FCSTD DOCUMENT  (FreeCAD 1.0R39109 (Git))
Label: Rotor_Mold_Assembly
License: All rights reserved
LicenseURL: http://en.wikipedia.org/wiki/All_rights_reserved
objects: App::Link×8, Part::FeaturePython×3, Spreadsheet::Sheet×1, App::Part×1
EXTERNAL_REF file=Rotor_Mold_Lid.FCStd obj=PocketBody
EXTERNAL_REF file=../../../Master_of_Puppets.FCStd obj=Alternator
EXTERNAL_REF file=../../../Master_of_Puppets.FCStd obj=Hub
EXTERNAL_REF file=../../../Master_of_Puppets.FCStd obj=Spreadsheet
EXTERNAL_REF file=Rotor_Mold_Base.FCStd obj=PolarPatternBody
EXTERNAL_REF file=Rotor_Mold_Surround.FCStd obj=PolarPatternBody
EXTERNAL_REF file=Rotor_Mold_Island.FCStd obj=PocketBody
EXTERNAL_REF file=../Rotor_Back.FCStd obj=Part
EXTERNAL_REF file=../../../Fasteners/Fastener_Bolt_HubHoles.FCStd obj=Binder
EXTERNAL_REF file=../../../Fasteners/Fastener_HexNut_HubHoles.FCStd obj=Binder
EXTERNAL_REF file=../../../Fasteners/Fastener_WoodScrew_RotorMold.FCStd obj=Part

FEATURE [App::Link] Link  label="Rotor_Mold_Lid"
  LinkPlacement = pos=(0,0,35) rot=(0,0,1;0rad)
  LinkedObject = -> <external Rotor_Mold_Lid.FCStd>#PocketBody
  Placement = pos=(0,0,35) rot=(0,0,1;0rad)
  expr: .Placement.Base.z = Spreadsheet.LidZ
  expr: Visibility = Spreadsheet.ShowLid
FEATURE [Spreadsheet::Sheet] Spreadsheet
  cells = A1='Inputs; A2='RotorDiskRadius; B2(RotorDiskRadius)==Master_of_Puppets#Spreadsheet.RotorDiskRadius; A3='MagnetThickness; B3(MagnetThickness)==Master_of_Puppets#Spreadsheet.MagnetThickness; A4='RotorDiskThickness; B4(RotorDiskThickness)==Master_of_Puppets#Spreadsheet.RotorDiskThickness; A5='HubPitchCircleRadius; B5(HubPitchCircleRadius)==Master_of_Puppets#Hub.HubPitchCircleRadius; A6='MagnetMaterial; B6(MagnetMaterial)==Master_of_Puppets#Spreadsheet.MagnetMaterial; A7='RotorMoldBaseThickness; B7(RotorMoldBaseThickness)==Master_of_Puppets#Alternator.RotorMoldBaseThickness; A8='NumberOfRotorMoldBolts; B8(NumberOfRotorMoldBolts)==Master_of_Puppets#Alternator.NumberOfRotorMoldBolts; A9='RotorMoldScrewHolesCircumradius; B9(RotorMoldScrewHolesCircumradius)==Master_of_Puppets#Alternator.RotorMoldScrewHolesCircumradius; A10='NumberOfRotorMoldScrews; B10(NumberOfRotorMoldScrews)==Master_of_Puppets#Alternator.NumberOfRotorMoldScrews; A11='RotorMoldSurroundThickness; B11(RotorMoldSurroundThickness)==Master_of_Puppets#Alternator.RotorMoldSurroundThickness; A12='RotorMoldScrewLength; B12(RotorMoldScrewLength)==Master_of_Puppets#Alternator.RotorMoldScrewLength; A13='Calculated; A14='DistanceBetweenLayers; B14(DistanceBetweenLayers)=0; C14='Increase to see space between parts.; A15='SurroundZ; B15(SurroundZ)==RotorMoldBaseThickness + DistanceBetweenLayers; A16='IslandZ; B16(IslandZ)==SurroundZ + RotorDiskThickness; A17='ScrewZ; B17(ScrewZ)==SurroundZ + RotorMoldSurroundThickness - RotorMoldScrewLength; A18='LidZ; B18(LidZ)==IslandZ + MagnetThickness + DistanceBetweenLayers; A19='ShowLid; B19(ShowLid)==MagnetMaterial != <<Ferrite C8>> ? 1 : 0; A20='NutsZ; B20(NutsZ)==ShowLid == 1 ? LidZ : SurroundZ + RotorMoldSurroundThickness
FEATURE [App::Link] Link001  label="Rotor_Mold_Base"
  LinkedObject = -> <external Rotor_Mold_Base.FCStd>#PolarPatternBody
FEATURE [App::Link] Link002  label="Rotor_Mold_Surround"
  LinkPlacement = pos=(0,0,15) rot=(0,0,1;0rad)
  LinkedObject = -> <external Rotor_Mold_Surround.FCStd>#PolarPatternBody
  Placement = pos=(0,0,15) rot=(0,0,1;0rad)
  expr: .Placement.Base.z = Spreadsheet.SurroundZ
FEATURE [App::Link] Link003  label="Rotor_Mold_Island"
  LinkPlacement = pos=(0,0,25) rot=(0,0,1;0rad)
  LinkedObject = -> <external Rotor_Mold_Island.FCStd>#PocketBody
  Placement = pos=(0,0,25) rot=(0,0,1;0rad)
  expr: .Placement.Base.z = Spreadsheet.IslandZ
FEATURE [App::Link] Link004  label="Rotor"
  LinkPlacement = pos=(0,0,15) rot=(0,0,1;0rad)
  LinkedObject = -> <external ../Rotor_Back.FCStd>#Part
  Placement = pos=(0,0,15) rot=(0,0,1;0rad)
  expr: .Placement.Base.z = Spreadsheet.SurroundZ
FEATURE [App::Link] Link005  label="Fastener_Bolt_HubHoles"
  LinkPlacement = pos=(0,50,0) rot=(0,0,1;0rad)
  LinkedObject = -> <external ../../../Fasteners/Fastener_Bolt_HubHoles.FCStd>#Binder
  Placement = pos=(0,50,0) rot=(0,0,1;0rad)
  Scale = -1
  ScaleVector = (-1,-1,-1)
  expr: .Placement.Base.y = Spreadsheet.HubPitchCircleRadius
FEATURE [Part::FeaturePython] Array  label="Bolts"  # Draft array (typed FeaturePython)
  AlwaysSyncPlacement = false
  Angle = 360
  ArrayType = 1
  Axis = (0,0,1)
  Base = -> Link005
  Center = (0,0,0)
  Count = 2
  ExpandArray = false
  Fuse = false
  IntervalAxis = (0,0,0)
  IntervalX = (50,0,0)
  IntervalY = (0,50,0)
  IntervalZ = (0,0,50)
  NumberCircles = 3
  NumberPolar = 2
  NumberX = 2
  NumberY = 2
  NumberZ = 1
  PlacementList = 2 placements: [(0,50,0),(-6.12323e-15,-50,0)]
  RadialDistance = 50
  ScaleList = (2) [(1,1,1),(1,1,1)]
  Symmetry = 1
  TangentialDistance = 25
  expr: NumberPolar = Spreadsheet.NumberOfRotorMoldBolts
FEATURE [App::Link] Link006  label="Fastener_HexNut"
  LinkPlacement = pos=(0,50,0) rot=(0,0,1;0rad)
  LinkedObject = -> <external ../../../Fasteners/Fastener_HexNut_HubHoles.FCStd>#Binder
  Placement = pos=(0,50,0) rot=(0,0,1;0rad)
  expr: .Placement.Base.y = Spreadsheet.HubPitchCircleRadius
FEATURE [Part::FeaturePython] Array001  label="Nuts"  # Draft array (typed FeaturePython)
  AlwaysSyncPlacement = false
  Angle = 360
  ArrayType = 1
  Axis = (0,0,1)
  Base = -> Link006
  Center = (0,0,0)
  Count = 2
  ExpandArray = false
  Fuse = false
  IntervalAxis = (0,0,0)
  IntervalX = (50,0,0)
  IntervalY = (0,50,0)
  IntervalZ = (0,0,50)
  NumberCircles = 3
  NumberPolar = 2
  NumberX = 2
  NumberY = 2
  NumberZ = 1
  Placement = pos=(0,0,35) rot=(0,0,1;0rad)
  PlacementList = 2 placements: [(0,50,0),(-6.12323e-15,-50,0)]
  RadialDistance = 50
  ScaleList = (2) [(1,1,1),(1,1,1)]
  Symmetry = 1
  TangentialDistance = 25
  expr: .Placement.Base.z = Spreadsheet.NutsZ
  expr: NumberPolar = Spreadsheet.NumberOfRotorMoldBolts
FEATURE [App::Link] Link007  label="Fastener_WoodScrew_RotorMold"
  LinkPlacement = pos=(0,176.7,0) rot=(0,0,1;0rad)
  LinkedObject = -> <external ../../../Fasteners/Fastener_WoodScrew_RotorMold.FCStd>#Part
  Placement = pos=(0,176.7,0) rot=(0,0,1;0rad)
  expr: .Placement.Base.y = Spreadsheet.RotorMoldScrewHolesCircumradius
  expr: .Placement.Base.z = Spreadsheet.ScrewZ
FEATURE [Part::FeaturePython] Array002  label="Screws"  # Draft array (typed FeaturePython)
  AlwaysSyncPlacement = false
  Angle = 360
  ArrayType = 1
  Axis = (0,0,1)
  Base = -> Link007
  Center = (0,0,0)
  Count = 9
  ExpandArray = false
  Fuse = false
  IntervalAxis = (0,0,0)
  IntervalX = (50,0,0)
  IntervalY = (0,50,0)
  IntervalZ = (0,0,50)
  NumberCircles = 3
  NumberPolar = 9
  NumberX = 2
  NumberY = 2
  NumberZ = 1
  PlacementList = 9 placements: [(0,176.7,0),(-113.581,135.36,0),(-174.016,30.6836,0),(-153.027,-88.35,0),(-60.435,-166.044,0),(60.435,-166.044,0),(153.027,-88.35,0),(174.016,30.6836,0),(113.581,135.36,0)]
  RadialDistance = 50
  ScaleList = (9) [(1,1,1),(1,1,1),(1,1,1),(1,1,1),(1,1,1),(1,1,1),(1,1,1),(1,1,1),(1,1,1)]
  Symmetry = 1
  TangentialDistance = 25
  expr: NumberPolar = Spreadsheet.NumberOfRotorMoldScrews
FEATURE [App::Part] Part  label="Rotor_Mold_Assembly"
  Group = -> [Link001,Link002,Link003,Link004,Link,Link005,Array,Link006,Array001,Link007,Array002]
  Origin = -> Origin

RESOLVED EXTERNAL PARTS (link-assembly join: the EXTERNAL_REF files above that resolve inside this repo's crawl, each included once):
---- part ../../../Fasteners/Fastener_Bolt_HubHoles.FCStd = doc fcstd_15687eb65cfb ----
FCSTD DOCUMENT  (FreeCAD 0.20R29177 (Git))
Label: Fastener_Bolt_HubHoles
License: All rights reserved
LicenseURL: http://en.wikipedia.org/wiki/All_rights_reserved
objects: PartDesign::SubShapeBinder×1
note: 1 computed .brp shape members not serialized (recipe doc carries the construction recipe); baked Part::Feature solids carry a one-line shape summary decoded from their .brp
EXTERNAL_REF file=Fastener_Bolt_Tail_Vane.FCStd obj=Body

FEATURE [PartDesign::SubShapeBinder] Binder  label="Fastener_Bolt_HubHoles"
  BindCopyOnChange = 2
  BindMode = 0
  ClaimChildren = false
  Fuse = false
  MakeFace = true
  OffsetFill = false
  OffsetIntersection = false
  OffsetJoinType = 0
  OffsetOpenResult = false
  PartialLoad = false
  Relative = true
  Support = -> [<external Fastener_Bolt_Tail_Vane.FCStd>#Body]
  Variant = 1
  _Version = 2
---- part ../../../Fasteners/Fastener_HexNut_HubHoles.FCStd = doc fcstd_dba15245a95b ----
FCSTD DOCUMENT  (FreeCAD 0.21R33771 (Git))
Label: Fastener_HexNut_HubHoles
License: All rights reserved
LicenseURL: http://en.wikipedia.org/wiki/All_rights_reserved
objects: PartDesign::SubShapeBinder×1
note: 1 computed .brp shape members not serialized (recipe doc carries the construction recipe); baked Part::Feature solids carry a one-line shape summary decoded from their .brp
EXTERNAL_REF file=Fastener_HexNut.FCStd obj=Body

FEATURE [PartDesign::SubShapeBinder] Binder  label="Fastener_HexNut"
  BindCopyOnChange = 2
  BindMode = 0
  ClaimChildren = false
  Fuse = false
  MakeFace = true
  OffsetFill = false
  OffsetIntersection = false
  OffsetJoinType = 0
  OffsetOpenResult = false
  PartialLoad = false
  Relative = true
  Support = -> [<external Fastener_HexNut.FCStd>#Body]
  Variant = 1
  _Version = 2
---- part ../../../Fasteners/Fastener_WoodScrew_RotorMold.FCStd = doc fcstd_a80e977c1a3f ----
FCSTD DOCUMENT  (FreeCAD 0.21R33771 (Git))
Label: Fastener_WoodScrew_RotorMold
Comment: DIN 571 Hexagon head wood screw
License: All rights reserved
LicenseURL: http://en.wikipedia.org/wiki/All_rights_reserved
objects: App::Link×1, PartDesign::SubShapeBinder×1, App::Part×1
note: 1 computed .brp shape members not serialized (recipe doc carries the construction recipe); baked Part::Feature solids carry a one-line shape summary decoded from their .brp
EXTERNAL_REF file=Fastener_WoodScrew_StatorMold.FCStd obj=Sweep
EXTERNAL_REF file=Fastener_WoodScrew_StatorMold.FCStd obj=Body

FEATURE [App::Link] Link  label="TipThreadLink"
  LinkedObject = -> <external Fastener_WoodScrew_StatorMold.FCStd>#Sweep
FEATURE [PartDesign::SubShapeBinder] Binder
  BindCopyOnChange = 2
  BindMode = 0
  ClaimChildren = false
  Context = -> Part [Binder.]
  Fuse = false
  MakeFace = true
  OffsetFill = false
  OffsetIntersection = false
  OffsetJoinType = 0
  OffsetOpenResult = false
  PartialLoad = false
  Relative = true
  Support = -> [<external Fastener_WoodScrew_StatorMold.FCStd>#Body]
  Variant = 1
  _Version = 2
FEATURE [App::Part] Part  label="Fastener_WoodScrew"
  Group = -> [Link,Binder]
  Origin = -> Origin
---- part ../../../Master_of_Puppets.FCStd = doc fcstd_6404554055c4 (61625 chars; too large to inline — full recipe in that document) ----
---- part ../Rotor_Back.FCStd = doc fcstd_8870bba639fa ----
FCSTD DOCUMENT  (FreeCAD 0.21R33675 (Git))
Label: Rotor_Back
License: All rights reserved
LicenseURL: http://en.wikipedia.org/wiki/All_rights_reserved
objects: App::Link×2, Spreadsheet::Sheet×1, App::Part×1
EXTERNAL_REF file=Rotor_Disk_Back.FCStd obj=Pocket001Body
EXTERNAL_REF file=../../Master_of_Puppets.FCStd obj=Alternator
EXTERNAL_REF file=../../Master_of_Puppets.FCStd obj=Spreadsheet
EXTERNAL_REF file=Rotor_Disk_Back_ReducedWeight.FCStd obj=Body
EXTERNAL_REF file=MagnetResin_Assembly.FCStd obj=Part

FEATURE [App::Link] Link  label="Rotor_Disk_Back"
  LinkPlacement = pos=(3.6e-15,0,0) rot=(0,0,1;0rad)
  LinkedObject = -> <external Rotor_Disk_Back.FCStd>#Pocket001Body
  Placement = pos=(3.6e-15,0,0) rot=(0,0,1;0rad)
  expr: LinkedObject = Spreadsheet.Disk
FEATURE [Spreadsheet::Sheet] Spreadsheet
  cells = A1='Inputs; A2='RotorDiskRadius; B2(RotorDiskRadius)==Master_of_Puppets#Spreadsheet.RotorDiskRadius; A3='WeightReductionRotorDiskRadiusThreshold; B3(WeightReductionRotorDiskRadiusThreshold)==Master_of_Puppets#Alternator.WeightReductionRotorDiskRadiusThreshold; A4='Disk; A5='DiskFullWeight; B5(DiskFullWeight)==<<Rotor_Disk_Back>>#<<Rotor_Disk_Back>>._self; A6='DiskReducedWeight; B6(DiskReducedWeight)==<<Rotor_Disk_Back_ReducedWeight>>#<<Rotor_Disk_Back>>._self; A7='Disk; B7(Disk)==RotorDiskRadius <= WeightReductionRotorDiskRadiusThreshold ? DiskFullWeight : DiskReducedWeight
FEATURE [App::Link] Link003  label="MagnetResin_Assembly"
  LinkedObject = -> <external MagnetResin_Assembly.FCStd>#Part
FEATURE [App::Part] Part  label="Rotor"
  Group = -> [Link,Link003]
  Origin = -> Origin
  Placement = pos=(0,0,0) rot=(0,1,0;3.14159rad)
---- part Rotor_Mold_Base.FCStd = doc fcstd_7ba465a5f749 ----
FCSTD DOCUMENT  (FreeCAD 0.20R29177 (Git))
Label: Rotor_Mold_Base
License: All rights reserved
LicenseURL: http://en.wikipedia.org/wiki/All_rights_reserved
objects: Sketcher::SketchObject×3, PartDesign::Pocket×2, PartDesign::PolarPattern×2, PartDesign::Pad×1, Spreadsheet::Sheet×1, PartDesign::Body×1
note: 12 computed .brp shape members not serialized (recipe doc carries the construction recipe); baked Part::Feature solids carry a one-line shape summary decoded from their .brp
EXTERNAL_REF file=../../../Master_of_Puppets.FCStd obj=Alternator
EXTERNAL_REF file=../../../Master_of_Puppets.FCStd obj=Hub
EXTERNAL_REF file=../../../Master_of_Puppets.FCStd obj=Spreadsheet

FEATURE [Sketcher::SketchObject] Sketch
  FullyConstrained = true
  MapMode = 5
  Support = -> [XY_Plane001]
  expr: Constraints[15] = Spreadsheet.RotorMoldSideLength
  sketch-geometry (6):
    g0: LineSegment StartX=-199.995 StartY=199.995 StartZ=0 EndX=199.995 EndY=199.995 EndZ=0
    g1: LineSegment StartX=199.995 StartY=199.995 StartZ=0 EndX=199.995 EndY=-199.995 EndZ=0
    g2: LineSegment StartX=199.995 StartY=-199.995 StartZ=0 EndX=-199.995 EndY=-199.995 EndZ=0
    g3: LineSegment StartX=-199.995 StartY=-199.995 StartZ=0 EndX=-199.995 EndY=199.995 EndZ=0
    g4: LineSegment StartX=-199.995 StartY=199.995 StartZ=0 EndX=199.995 EndY=-199.995 EndZ=0
    g5: LineSegment StartX=199.995 StartY=199.995 StartZ=0 EndX=-199.995 EndY=-199.995 EndZ=0
  constraints (16):
    c: Coincident(g0,g1)
    c: Coincident(g1,g2)
    c: Coincident(g2,g3)
    c: Coincident(g3,g0)
    c: Horizontal(g0)
    c: Horizontal(g2)
    c: Vertical(g1)
    c: Vertical(g3)
    c: Coincident(g4,g0)
    c: Coincident(g4,g1)
    c: Coincident(g5,g0)
    c: Coincident(g5,g2)
    c: PointOnObject(g-1,g5)
    c: PointOnObject(g-1,g4)
    c: Equal(g0,g3)
    c: Distance(g0) = 399.99
FEATURE [PartDesign::Pad] Pad
  AllowMultiFace = false
  Direction = (0,0,1)
  Length = 15
  Length2 = 100
  Profile = -> Sketch
  Type = 0
  expr: Length = Spreadsheet.RotorMoldBaseThickness
FEATURE [Sketcher::SketchObject] Sketch001  label="BoltHoleSketch"
  FullyConstrained = true
  MapMode = 5
  Placement = pos=(0,0,15) rot=(0,0,1;0rad)
  Support = -> [Pad]
  expr: Constraints[1] = Spreadsheet.HubPitchCircleRadius
  expr: Constraints[4] = Spreadsheet.HubHolesRadius
  sketch-geometry (2):
    g0: Circle CenterX=0 CenterY=0 CenterZ=0 NormalX=0 NormalY=0 NormalZ=1 AngleXU=0 Radius=50
    g1: Circle CenterX=0 CenterY=50 CenterZ=0 NormalX=0 NormalY=0 NormalZ=1 AngleXU=0 Radius=6
  constraints (5):
    c: Coincident(g0,g-1)
    c: Radius(g0) = 50
    c: PointOnObject(g1,g-2)
    c: PointOnObject(g1,g0)
    c: Radius(g1) = 6
FEATURE [PartDesign::Pocket] Pocket  label="BoltHolePocket"
  AllowMultiFace = false
  BaseFeature = -> Pad
  Direction = (0,0,-1)
  Length = 5
  Length2 = 100
  Profile = -> Sketch001
  Type = 1
FEATURE [Sketcher::SketchObject] Sketch002  label="ScrewHoleSketch"
  FullyConstrained = true
  MapMode = 5
  Placement = pos=(0,0,15) rot=(0,0,1;0rad)
  Support = -> [Pocket]
  expr: Constraints[1] = Spreadsheet.RotorMoldScrewHolesCircumradius
  expr: Constraints[3] = Spreadsheet.ScrewHoleRadius
  sketch-geometry (2):
    g0: Circle CenterX=0 CenterY=0 CenterZ=0 NormalX=0 NormalY=0 NormalZ=1 AngleXU=0 Radius=177
    g1: Circle CenterX=0 CenterY=177 CenterZ=0 NormalX=0 NormalY=0 NormalZ=1 AngleXU=0 Radius=2
  constraints (5):
    c: Coincident(g0,g-1)
    c: Radius(g0) = 177
    c: PointOnObject(g1,g0)
    c: Radius(g1) = 2
    c: PointOnObject(g1,g-2)
FEATURE [PartDesign::Pocket] Pocket001  label="ScrewHolePocket"
  AllowMultiFace = false
  BaseFeature = -> Pocket
  Direction = (0,0,-1)
  Length = 5
  Length2 = 100
  Profile = -> Sketch002
  Type = 1
FEATURE [PartDesign::PolarPattern] PolarPattern  label="ScrewHolePolarPattern"
  Angle = 360
  Axis = -> Sketch002 [N_Axis]
  BaseFeature = -> Pocket001
  Occurrences = 16
  Originals = -> [Pocket001]
  expr: Occurrences = Spreadsheet.NumberOfRotorMoldScrews
FEATURE [Spreadsheet::Sheet] Spreadsheet
  cells = A1=Inputs; A2=RotorDiskRadius; B2(RotorDiskRadius)==Master_of_Puppets#Spreadsheet.RotorDiskRadius; A3=HubHolesRadius; B3(HubHolesRadius)==Master_of_Puppets#Hub.HubHolesRadius; A4=HubPitchCircleRadius; B4(HubPitchCircleRadius)==Master_of_Puppets#Hub.HubPitchCircleRadius; A5=ScrewHoleRadius; B5(ScrewHoleRadius)==Master_of_Puppets#Alternator.ScrewHoleRadius; A6=RotorMoldSideLength; B6(RotorMoldSideLength)==Master_of_Puppets#Alternator.RotorMoldSideLength; A7=NumberOfRotorMoldScrews; B7(NumberOfRotorMoldScrews)==Master_of_Puppets#Alternator.NumberOfRotorMoldScrews; A8=RotorMoldScrewHolesCircumradius; B8(RotorMoldScrewHolesCircumradius)==Master_of_Puppets#Alternator.RotorMoldScrewHolesCircumradius; A9=NumberOfRotorMoldBolts; B9(NumberOfRotorMoldBolts)==Master_of_Puppets#Alternator.NumberOfRotorMoldBolts; A10=RotorMoldBaseThickness; B10(RotorMoldBaseThickness)==Master_of_Puppets#Alternator.RotorMoldBaseThickness
FEATURE [PartDesign::PolarPattern] PolarPattern001  label="BoltHolePolarPattern"
  Angle = 360
  Axis = -> Sketch001 [N_Axis]
  BaseFeature = -> PolarPattern
  Occurrences = 2
  Originals = -> [Pocket]
  expr: Occurrences = Spreadsheet.NumberOfRotorMoldBolts
FEATURE [PartDesign::Body] PolarPatternBody  label="Rotor_Mold_Base"
  Group = -> [Sketch,Pad,Sketch001,Pocket,Sketch002,Pocket001,PolarPattern,PolarPattern001]
  Openafpm_Flat = true
  Origin = -> Origin001
  Tip = -> PolarPattern001
---- part Rotor_Mold_Island.FCStd = doc fcstd_08897b0bbb15 ----
FCSTD DOCUMENT  (FreeCAD 0.20R29177 (Git))
Label: Rotor_Mold_Island
License: All rights reserved
LicenseURL: http://en.wikipedia.org/wiki/All_rights_reserved
objects: Sketcher::SketchObject×2, PartDesign::Pad×1, PartDesign::Pocket×1, Spreadsheet::Sheet×1, PartDesign::PolarPattern×1, PartDesign::Body×1
note: 8 computed .brp shape members not serialized (recipe doc carries the construction recipe); baked Part::Feature solids carry a one-line shape summary decoded from their .brp
EXTERNAL_REF file=../../../Master_of_Puppets.FCStd obj=Alternator
EXTERNAL_REF file=../../../Master_of_Puppets.FCStd obj=Hub
EXTERNAL_REF file=../../../Master_of_Puppets.FCStd obj=Spreadsheet

FEATURE [Sketcher::SketchObject] Sketch
  FullyConstrained = true
  MapMode = 5
  Support = -> [XY_Plane001]
  expr: Constraints[1] = Spreadsheet.IslandRadius
  sketch-geometry (1):
    g0: Circle CenterX=0 CenterY=0 CenterZ=0 NormalX=0 NormalY=0 NormalZ=1 AngleXU=0 Radius=77
  constraints (2):
    c: Coincident(g0,g-1)
    c: Radius(g0) = 77
FEATURE [PartDesign::Pad] Pad
  AllowMultiFace = false
  Direction = (0,0,1)
  Length = 10
  Length2 = 100
  Profile = -> Sketch
  Type = 0
  expr: Length = Spreadsheet.RotorMoldIslandThickness
FEATURE [Sketcher::SketchObject] Sketch001
  FullyConstrained = true
  MapMode = 5
  Placement = pos=(0,0,10) rot=(0,0,1;0rad)
  Support = -> [Pad]
  expr: Constraints[3] = Spreadsheet.HubPitchCircleRadius
  expr: Constraints[4] = Spreadsheet.HubHolesRadius
  sketch-geometry (2):
    g0: LineSegment StartX=0 StartY=50 StartZ=0 EndX=0 EndY=0 EndZ=0
    g1: Circle CenterX=0 CenterY=50 CenterZ=0 NormalX=0 NormalY=0 NormalZ=1 AngleXU=0 Radius=6
  constraints (5):
    c: Coincident(g0,g-1)
    c: Vertical(g0)
    c: Coincident(g1,g0)
    c: Distance(g0) = 50
    c: Radius(g1) = 6
FEATURE [PartDesign::Pocket] Pocket
  AllowMultiFace = false
  BaseFeature = -> Pad
  Direction = (0,0,-1)
  Length = 5
  Length2 = 100
  Profile = -> Sketch001
  Type = 1
FEATURE [Spreadsheet::Sheet] Spreadsheet
  cells = A1=Inputs; A2=HubHolesRadius; B2(HubHolesRadius)==Master_of_Puppets#Hub.HubHolesRadius; A3=HubPitchCircleRadius; B3(HubPitchCircleRadius)==Master_of_Puppets#Hub.HubPitchCircleRadius; A4=MagnetThickness; B4(MagnetThickness)==Master_of_Puppets#Spreadsheet.MagnetThickness; A5=IslandRadius; B5(IslandRadius)==Master_of_Puppets#Alternator.IslandRadius; A6=NumberOfRotorMoldBolts; B6(NumberOfRotorMoldBolts)==Master_of_Puppets#Alternator.NumberOfRotorMoldBolts; A7=RotorMoldIslandThickness; B7(RotorMoldIslandThickness)==Master_of_Puppets#Alternator.RotorMoldIslandThickness
FEATURE [PartDesign::PolarPattern] PolarPattern
  Angle = 360
  Axis = -> Sketch001 [N_Axis]
  BaseFeature = -> Pocket
  Occurrences = 2
  Originals = -> [Pocket]
  expr: Occurrences = Spreadsheet.NumberOfRotorMoldBolts
FEATURE [PartDesign::Body] PocketBody  label="Rotor_Mold_Island"
  Group = -> [Sketch,Pad,Sketch001,Pocket,PolarPattern]
  Openafpm_Flat = true
  Origin = -> Origin001
  Tip = -> PolarPattern
---- part Rotor_Mold_Lid.FCStd = doc fcstd_4d45015cea57 ----
FCSTD DOCUMENT  (FreeCAD 0.20R29177 (Git))
Label: Rotor_Mold_Lid
License: All rights reserved
LicenseURL: http://en.wikipedia.org/wiki/All_rights_reserved
objects: Sketcher::SketchObject×2, PartDesign::Pad×1, PartDesign::Pocket×1, Spreadsheet::Sheet×1, PartDesign::PolarPattern×1, PartDesign::Body×1
note: 8 computed .brp shape members not serialized (recipe doc carries the construction recipe); baked Part::Feature solids carry a one-line shape summary decoded from their .brp
EXTERNAL_REF file=../../../Master_of_Puppets.FCStd obj=Alternator
EXTERNAL_REF file=../../../Master_of_Puppets.FCStd obj=Fastener
EXTERNAL_REF file=../../../Master_of_Puppets.FCStd obj=Hub
EXTERNAL_REF file=../../../Master_of_Puppets.FCStd obj=Spreadsheet

FEATURE [Sketcher::SketchObject] Sketch
  FullyConstrained = true
  MapMode = 5
  Support = -> [XY_Plane001]
  expr: Constraints[15] = Spreadsheet.RotorMoldSideLength
  sketch-geometry (6):
    g0: LineSegment StartX=-199.995 StartY=199.995 StartZ=0 EndX=199.995 EndY=199.995 EndZ=0
    g1: LineSegment StartX=199.995 StartY=199.995 StartZ=0 EndX=199.995 EndY=-199.995 EndZ=0
    g2: LineSegment StartX=199.995 StartY=-199.995 StartZ=0 EndX=-199.995 EndY=-199.995 EndZ=0
    g3: LineSegment StartX=-199.995 StartY=-199.995 StartZ=0 EndX=-199.995 EndY=199.995 EndZ=0
    g4: LineSegment StartX=-199.995 StartY=199.995 StartZ=0 EndX=199.995 EndY=-199.995 EndZ=0
    g5: LineSegment StartX=199.995 StartY=199.995 StartZ=0 EndX=-199.995 EndY=-199.995 EndZ=0
  constraints (16):
    c: Coincident(g0,g1)
    c: Coincident(g1,g2)
    c: Coincident(g2,g3)
    c: Coincident(g3,g0)
    c: Horizontal(g0)
    c: Horizontal(g2)
    c: Vertical(g1)
    c: Vertical(g3)
    c: Coincident(g4,g0)
    c: Coincident(g4,g1)
    c: Coincident(g5,g0)
    c: Coincident(g5,g2)
    c: PointOnObject(g-1,g5)
    c: PointOnObject(g-1,g4)
    c: Equal(g0,g3)
    c: Distance(g0) = 399.99
FEATURE [PartDesign::Pad] Pad
  AllowMultiFace = false
  Direction = (0,0,1)
  Length = 6
  Length2 = 100
  Profile = -> Sketch
  Type = 0
  expr: Length = Spreadsheet.RotorMoldLidThickness
FEATURE [Sketcher::SketchObject] Sketch001
  FullyConstrained = true
  MapMode = 5
  Placement = pos=(0,0,6) rot=(0,0,1;0rad)
  Support = -> [Pad]
  expr: Constraints[1] = Spreadsheet.HubPitchCircleRadius
  expr: Constraints[4] = Spreadsheet.HoleRadius
  sketch-geometry (2):
    g0: Circle CenterX=0 CenterY=0 CenterZ=0 NormalX=0 NormalY=0 NormalZ=1 AngleXU=0 Radius=50
    g1: Circle CenterX=0 CenterY=50 CenterZ=0 NormalX=0 NormalY=0 NormalZ=1 AngleXU=0 Radius=15.39
  constraints (5):
    c: Coincident(g0,g-1)
    c: Radius(g0) = 50
    c: PointOnObject(g1,g-2)
    c: PointOnObject(g1,g0)
    c: Radius(g1) = 15.39
FEATURE [PartDesign::Pocket] Pocket
  AllowMultiFace = false
  BaseFeature = -> Pad
  Direction = (0,0,-1)
  Length = 5
  Length2 = 100
  Profile = -> Sketch001
  Type = 1
FEATURE [Spreadsheet::Sheet] Spreadsheet
  cells = A1=Inputs; A2=RotorDiskRadius; B2(RotorDiskRadius)==Master_of_Puppets#Spreadsheet.RotorDiskRadius; A3=HubPitchCircleRadius; B3(HubPitchCircleRadius)==Master_of_Puppets#Hub.HubPitchCircleRadius; A4=RotorMoldSideLength; B4(RotorMoldSideLength)==Master_of_Puppets#Alternator.RotorMoldSideLength; A5=NumberOfRotorMoldBolts; B5(NumberOfRotorMoldBolts)==Master_of_Puppets#Alternator.NumberOfRotorMoldBolts; A6=HubHolesWidthAcrossCorners; B6(HubHolesWidthAcrossCorners)==Master_of_Puppets#Fastener.HubHolesWidthAcrossCorners; A7=RotorMoldLidThickness; B7(RotorMoldLidThickness)==Master_of_Puppets#Alternator.RotorMoldLidThickness; A8=Calculations; A9=HoleRadiusPadding; B9(HoleRadiusPadding)=5; C9=Add space on either side of bolt head so that resin can flow out.; A10=HoleRadius; B10(HoleRadius)==HubHolesWidthAcrossCorners / 2 + HoleRadiusPadding
FEATURE [PartDesign::PolarPattern] PolarPattern001
  Angle = 360
  Axis = -> Sketch001 [N_Axis]
  BaseFeature = -> Pocket
  Occurrences = 2
  Originals = -> [Pocket]
  expr: Occurrences = Spreadsheet.NumberOfRotorMoldBolts
FEATURE [PartDesign::Body] PocketBody  label="Rotor_Mold_Lid"
  Group = -> [Sketch,Pad,Sketch001,Pocket,PolarPattern001]
  Openafpm_Flat = true
  Origin = -> Origin001
  Tip = -> PolarPattern001
---- part Rotor_Mold_Surround.FCStd = doc fcstd_e290a8b8365a ----
FCSTD DOCUMENT  (FreeCAD 0.20R29177 (Git))
Label: Rotor_Mold_Surround
License: All rights reserved
LicenseURL: http://en.wikipedia.org/wiki/All_rights_reserved
objects: Sketcher::SketchObject×3, PartDesign::Pocket×2, PartDesign::Pad×1, PartDesign::PolarPattern×1, Spreadsheet::Sheet×1, PartDesign::Body×1
note: 11 computed .brp shape members not serialized (recipe doc carries the construction recipe); baked Part::Feature solids carry a one-line shape summary decoded from their .brp
EXTERNAL_REF file=../../../Master_of_Puppets.FCStd obj=Alternator
EXTERNAL_REF file=../../../Master_of_Puppets.FCStd obj=Spreadsheet

FEATURE [Sketcher::SketchObject] Sketch
  FullyConstrained = true
  MapMode = 5
  Support = -> [XY_Plane001]
  expr: Constraints[15] = Spreadsheet.RotorMoldSideLength
  sketch-geometry (6):
    g0: LineSegment StartX=-199.995 StartY=199.995 StartZ=0 EndX=199.995 EndY=199.995 EndZ=0
    g1: LineSegment StartX=199.995 StartY=199.995 StartZ=0 EndX=199.995 EndY=-199.995 EndZ=0
    g2: LineSegment StartX=199.995 StartY=-199.995 StartZ=0 EndX=-199.995 EndY=-199.995 EndZ=0
    g3: LineSegment StartX=-199.995 StartY=-199.995 StartZ=0 EndX=-199.995 EndY=199.995 EndZ=0
    g4: LineSegment StartX=-199.995 StartY=199.995 StartZ=0 EndX=199.995 EndY=-199.995 EndZ=0
    g5: LineSegment StartX=199.995 StartY=199.995 StartZ=0 EndX=-199.995 EndY=-199.995 EndZ=0
  constraints (16):
    c: Coincident(g0,g1)
    c: Coincident(g1,g2)
    c: Coincident(g2,g3)
    c: Coincident(g3,g0)
    c: Horizontal(g0)
    c: Horizontal(g2)
    c: Vertical(g1)
    c: Vertical(g3)
    c: Coincident(g4,g0)
    c: Coincident(g4,g1)
    c: Coincident(g5,g0)
    c: Coincident(g5,g2)
    c: PointOnObject(g-1,g5)
    c: PointOnObject(g-1,g4)
    c: Equal(g0,g3)
    c: Distance(g0) = 399.99
FEATURE [PartDesign::Pad] Pad
  AllowMultiFace = false
  Direction = (0,0,1)
  Length = 20
  Length2 = 100
  Profile = -> Sketch
  Type = 0
  expr: Length = Spreadsheet.RotorMoldSurroundThickness
FEATURE [Sketcher::SketchObject] Sketch001  label="CenterHoleSketch"
  FullyConstrained = true
  MapMode = 5
  Placement = pos=(0,0,20) rot=(0,0,1;0rad)
  Support = -> [Pad]
  expr: Constraints[1] = Spreadsheet.RotorMoldSurroundRadius
  sketch-geometry (1):
    g0: Circle CenterX=0 CenterY=0 CenterZ=0 NormalX=0 NormalY=0 NormalZ=1 AngleXU=0 Radius=155
  constraints (2):
    c: Coincident(g0,g-1)
    c: Radius(g0) = 155
FEATURE [PartDesign::Pocket] Pocket  label="CenterHolePocket"
  AllowMultiFace = false
  BaseFeature = -> Pad
  Direction = (0,0,-1)
  Length = 5
  Length2 = 100
  Profile = -> Sketch001
  Type = 1
FEATURE [Sketcher::SketchObject] Sketch002  label="ScrewHoleSketch"
  FullyConstrained = true
  MapMode = 5
  Placement = pos=(0,0,20) rot=(0,0,1;0rad)
  Support = -> [Pocket]
  expr: Constraints[1] = Spreadsheet.RotorMoldScrewHolesCircumradius
  expr: Constraints[2] = Spreadsheet.ScewHoleRadius
  sketch-geometry (1):
    g0: Circle CenterX=0 CenterY=177 CenterZ=0 NormalX=0 NormalY=0 NormalZ=1 AngleXU=0 Radius=2
  constraints (3):
    c: PointOnObject(g0,g-2)
    c: DistanceY(g-1,g0) = 177
    c: Radius(g0) = 2
FEATURE [PartDesign::Pocket] Pocket001  label="ScrewHolePocket"
  AllowMultiFace = false
  BaseFeature = -> Pocket
  Direction = (0,0,-1)
  Length = 5
  Length2 = 100
  Profile = -> Sketch002
  Type = 1
FEATURE [PartDesign::PolarPattern] PolarPattern  label="ScrewHolePolarPattern"
  Angle = 360
  Axis = -> Sketch002 [N_Axis]
  BaseFeature = -> Pocket001
  Occurrences = 16
  Originals = -> [Pocket001]
  expr: Occurrences = Spreadsheet.NumberOfRotorMoldScrews
FEATURE [Spreadsheet::Sheet] Spreadsheet
  cells = A1=Inputs; A2=RotorDiskRadius; B2(RotorDiskRadius)==Master_of_Puppets#Spreadsheet.RotorDiskRadius; A3=MagnetThickness; B3(MagnetThickness)==Master_of_Puppets#Spreadsheet.MagnetThickness; A4=RotorDiskThickness; B4(RotorDiskThickness)==Master_of_Puppets#Spreadsheet.RotorDiskThickness; A5=ScewHoleRadius; B5(ScewHoleRadius)==Master_of_Puppets#Alternator.ScrewHoleRadius; A6=NumberOfRotorMoldScrews; B6(NumberOfRotorMoldScrews)==Master_of_Puppets#Alternator.NumberOfRotorMoldScrews; A7=RotorMoldSideLength; B7(RotorMoldSideLength)==Master_of_Puppets#Alternator.RotorMoldSideLength; A8=RotorMoldScrewHolesCircumradius; B8(RotorMoldScrewHolesCircumradius)==Master_of_Puppets#Alternator.RotorMoldScrewHolesCircumradius; A9=RotorMoldSurroundThickness; B9(RotorMoldSurroundThickness)==Master_of_Puppets#Alternator.RotorMoldSurroundThickness; A10=RotorMoldSurroundRadius; B10(RotorMoldSurroundRadius)==Master_of_Puppets#Alternator.RotorMoldSurroundRadius
FEATURE [PartDesign::Body] PolarPatternBody  label="Rotor_Mold_Surround"
  Group = -> [Sketch,Pad,Sketch001,Pocket,Sketch002,Pocket001,PolarPattern]
  Openafpm_Flat = true
  Origin = -> Origin001
  Tip = -> PolarPattern
